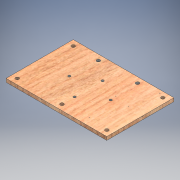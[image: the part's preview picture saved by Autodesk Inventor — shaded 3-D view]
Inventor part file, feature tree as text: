
AUTODESK INVENTOR PART (.ipt)
format: ipt  version: 2018 (Build 220112000, 112)  size: 146,432 bytes
history: native  units: mm
features: extrude x1
ambient origin geometry x8: Origin, YZ Plane, XZ Plane, XY Plane, X Axis, Y Axis, Z Axis, Center Point
bodies: Solid1 (feature_tree)
feature tree (1):
  extrude  "Extrusion1"  Depth=140.0mm
